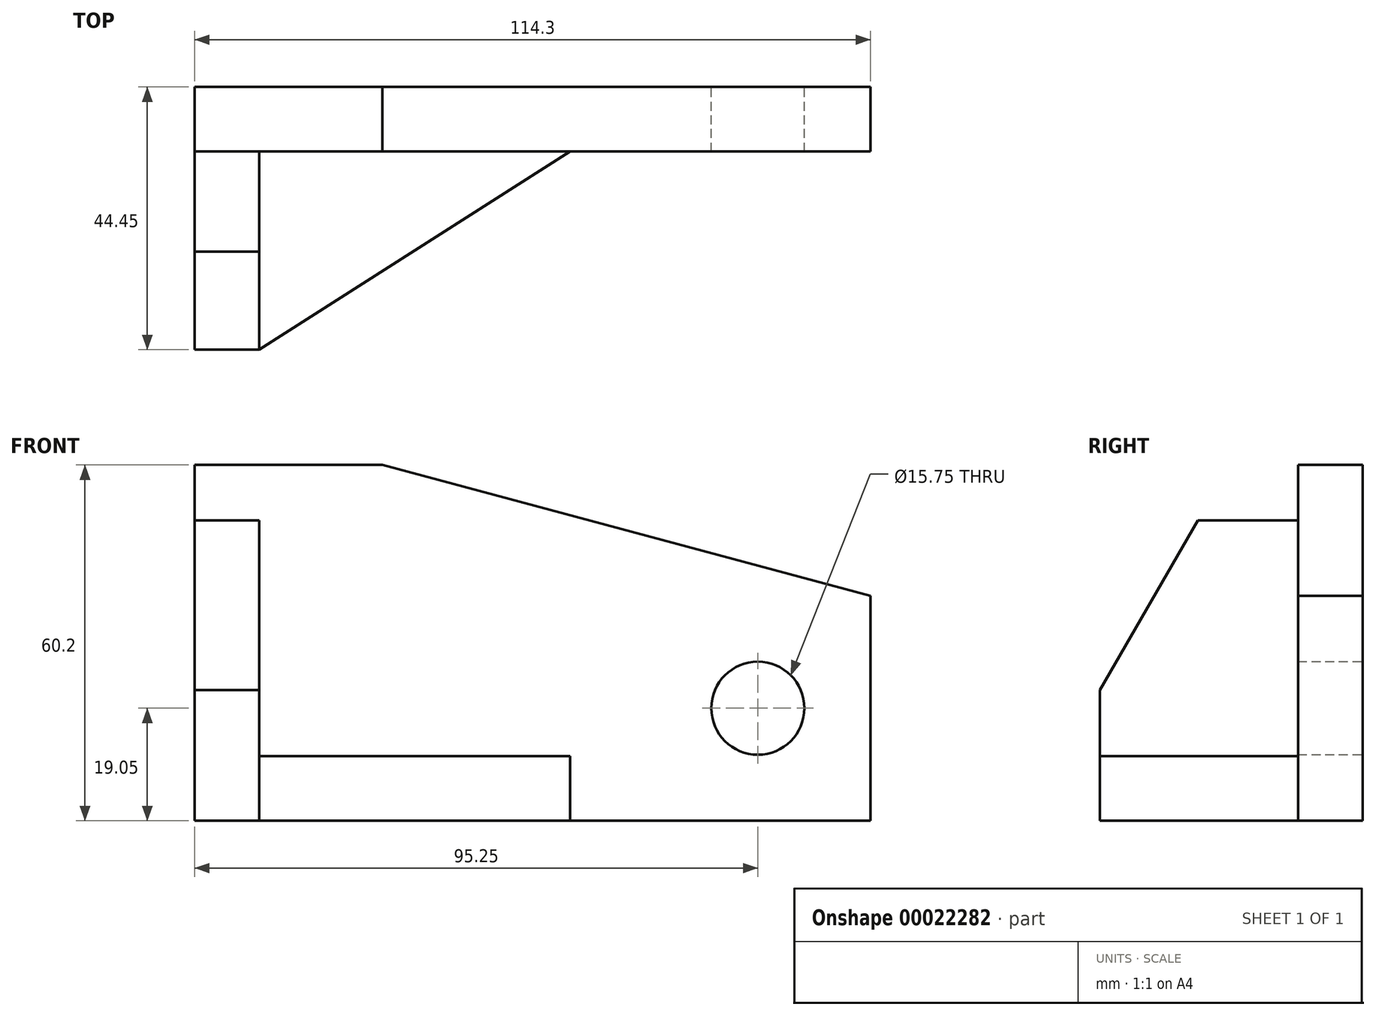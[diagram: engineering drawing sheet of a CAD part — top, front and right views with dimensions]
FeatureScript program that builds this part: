
annotation { "Feature Type Name" : "Feature", "Feature Type Description" : "" }
export const myFeature = defineFeature(function(context is Context, id is Id, definition is map)
    precondition{}
    {
        {
            var Q0;
            Q0=qCreatedBy(makeId("Front.planeOp"),FACE);
            var sketch = newSketch(context, id + "F0", { "sketchPlane" : qUnion([Q0])});
            skLineSegment(sketch, "E0.bottom", {"start": v(0, 0) * mm, "end": v(-114.3, 0) * mm});
            skLineSegment(sketch, "E0.top", {"start": v(0, 60.2) * mm, "end": v(-114.3, 60.2) * mm});
            skLineSegment(sketch, "E0.left", {"start": v(0, 0) * mm, "end": v(0, 60.2) * mm});
            skLineSegment(sketch, "E0.right", {"start": v(-114.3, 0) * mm, "end": v(-114.3, 60.2) * mm});
            skLineSegment(sketch, "E1", {"start": v(-82.55, 60.2) * mm, "end": v(0, 38.08) * mm});
            skCircle(sketch, "E2", {"center": v(-19.05, 19.05) * mm, "radius": 7.87 * mm});
            skSolve(sketch);
        }
        {
            var Q0;
            {var subQ3=sQuery(id+"F0.wireOp",EDGE,"E0.bottom");Q0=makeQuery(id+"F0.imprint","IMPRINT",FACE,{"disambiguationData":[TD([[makeQuery(id+"F0.imprint","IMPRINT",EDGE,{"derivedFrom":subQ3}),-1.0]])]});}
            extrude(context, id + "F1", {"entities" : qUnion([Q0]), "depth" : 10.92 * mm});
        }
        {
            var Q0;
            Q0=makeQuery(id+"F1.opExtrude","SWEPT_FACE",FACE,{"disambiguationData":[OSD([sQuery(id+"F0.wireOp",EDGE,"E0.right")])]});
            var sketch = newSketch(context, id + "F2", { "sketchPlane" : qUnion([Q0])});
            skLineSegment(sketch, "E3.bottom", {"start": v(10.92, 0) * mm, "end": v(44.45, 0) * mm});
            skLineSegment(sketch, "E3.top", {"start": v(10.92, 50.8) * mm, "end": v(44.45, 50.8) * mm});
            skLineSegment(sketch, "E3.left", {"start": v(10.92, 0) * mm, "end": v(10.92, 50.8) * mm});
            skLineSegment(sketch, "E3.right", {"start": v(44.45, 0) * mm, "end": v(44.45, 50.8) * mm});
            skLineSegment(sketch, "E4", {"start": v(27.88, 50.8) * mm, "end": v(44.45, 22.1) * mm});
            skSolve(sketch);
        }
        {
            var Q0;
            {var subQ2=sQuery(id+"F2.wireOp",EDGE,"E3.bottom");Q0=makeQuery(id+"F2.imprint","IMPRINT",FACE,{"disambiguationData":[TD([[makeQuery(id+"F2.imprint","IMPRINT",EDGE,{"derivedFrom":subQ2}),1.0]])]});}
            extrude(context, id + "F3", {"entities" : qUnion([Q0]), "operationType" : NewBodyOperationType.ADD, "oppositeDirection" : true, "depth" : 10.92 * mm});
        }
        {
            var Q0;
            Q0=makeQuery(id+"F3.boolean.opBoolean","MERGE",FACE,{"derivedFrom":[makeQuery(id+"F1.opExtrude","SWEPT_FACE",FACE,{"disambiguationData":[OSD([sQuery(id+"F0.wireOp",EDGE,"E0.bottom")])]}),makeQuery(id+"F3.opExtrude","SWEPT_FACE",FACE,{"disambiguationData":[OSD([sQuery(id+"F2.wireOp",EDGE,"E3.bottom")])]})]});
            var sketch = newSketch(context, id + "F4", { "sketchPlane" : qUnion([Q0])});
            skLineSegment(sketch, "E5.bottom", {"start": v(-103.38, 10.92) * mm, "end": v(-50.8, 10.92) * mm});
            skLineSegment(sketch, "E5.top", {"start": v(-103.38, 44.45) * mm, "end": v(-50.8, 44.45) * mm});
            skLineSegment(sketch, "E5.left", {"start": v(-103.38, 10.92) * mm, "end": v(-103.38, 44.45) * mm});
            skLineSegment(sketch, "E5.right", {"start": v(-50.8, 10.92) * mm, "end": v(-50.8, 44.45) * mm});
            skLineSegment(sketch, "E6", {"start": v(-103.38, 44.45) * mm, "end": v(-50.8, 10.92) * mm});
            skSolve(sketch);
        }
        {
            var Q0;
            Q0=makeQuery(id+"F4.imprint","IMPRINT",FACE,{"disambiguationData":[TD([[makeQuery(id+"F4.imprint","IMPRINT",EDGE,{"derivedFrom":sQuery(id+"F4.wireOp",EDGE,"E5.bottom")}),-1.0]])]});
            extrude(context, id + "F5", {"entities" : qUnion([Q0]), "oppositeDirection" : true, "depth" : 10.92 * mm});
        }
    });
